# Revit family: Door-Casement-Duratherm-Out_Swing-Wood
name_source: partatom
category: Doors
revit_build: Autodesk Revit 2017 (Build: 20190508_0315(x64)
units: mm (PartAtom-declared; Revit-internal decimal feet)

## family parameters
Always vertical = Yes
Cut with Voids When Loaded = No
Host = Wall
OmniClass Number = 23.30.10.00
OmniClass Title = Doors
Room Calculation Point = No
Shared = No

## types (2) — shared parameters
2D Width = 30"
Air Leakage = 0.05
Analytic Construction = <None>
Assembly Code = B2030900
Description = Outswing Door
Edition number = 1
Frame Material = Wood - Duratherm - Sapele Mahogany
Function = Exterior
Glazing = Low E
Glazing Material = Glass ‐ Duratherm ‐ Solarban 60
Handle bar height = 40"
Heat Transfer Coefficient (U) = 0.33 BTU/(h·ft²·°F)
Height = 74"
Manufacturer = Duratherm Window Corporation
Maximum Recommended Height = 120"
Maximum Recommended Width = 48"
Minimum Recommended Height = 74"
Minimum Recommended Width = 24"
Model = Outswing
Operation = Sliding
Panel Height = 70 3/4"
Panel Width = 24 1/4"
Panel Width 2 = 26 1/4"
Product Documentation Link = http://www.durathermwindows.com
Product Guid = 2b031f90-dc9f-4e7e-aac2-567f2570138c
Product data url = https://bimobject.com
Rough Height = 74 1/2"
Rough Width = 31"
Screen Height = 71 59/64"
Screen Width = 27 3/4"
Size Restrictions = Sizes are available outside of the recommended maximum values, but please contact Duratherm to confirm availability
Solar Heat Gain Coefficient = 0.38
Style = Hinged
Thermal Resistance (R) = 3.0300 (h·ft²·°F)/BTU
Thickness = 2 1/4"
URL = www.durathermwindow.com
Visual Light Transmittance = 0.7
Wall Closure = By host
Width = 30"
zero-valued in all types: Cost

## per-type parameters (varying)
| type | Screen Required | Screen not Required |
| Custom Size without Screen | No | Yes |
| Custom Size with Screen | Yes | No |

## geometry (parser evidence)
native form markers: Blend x6, Sweep x11
no freeform markers — native parametric forms only
